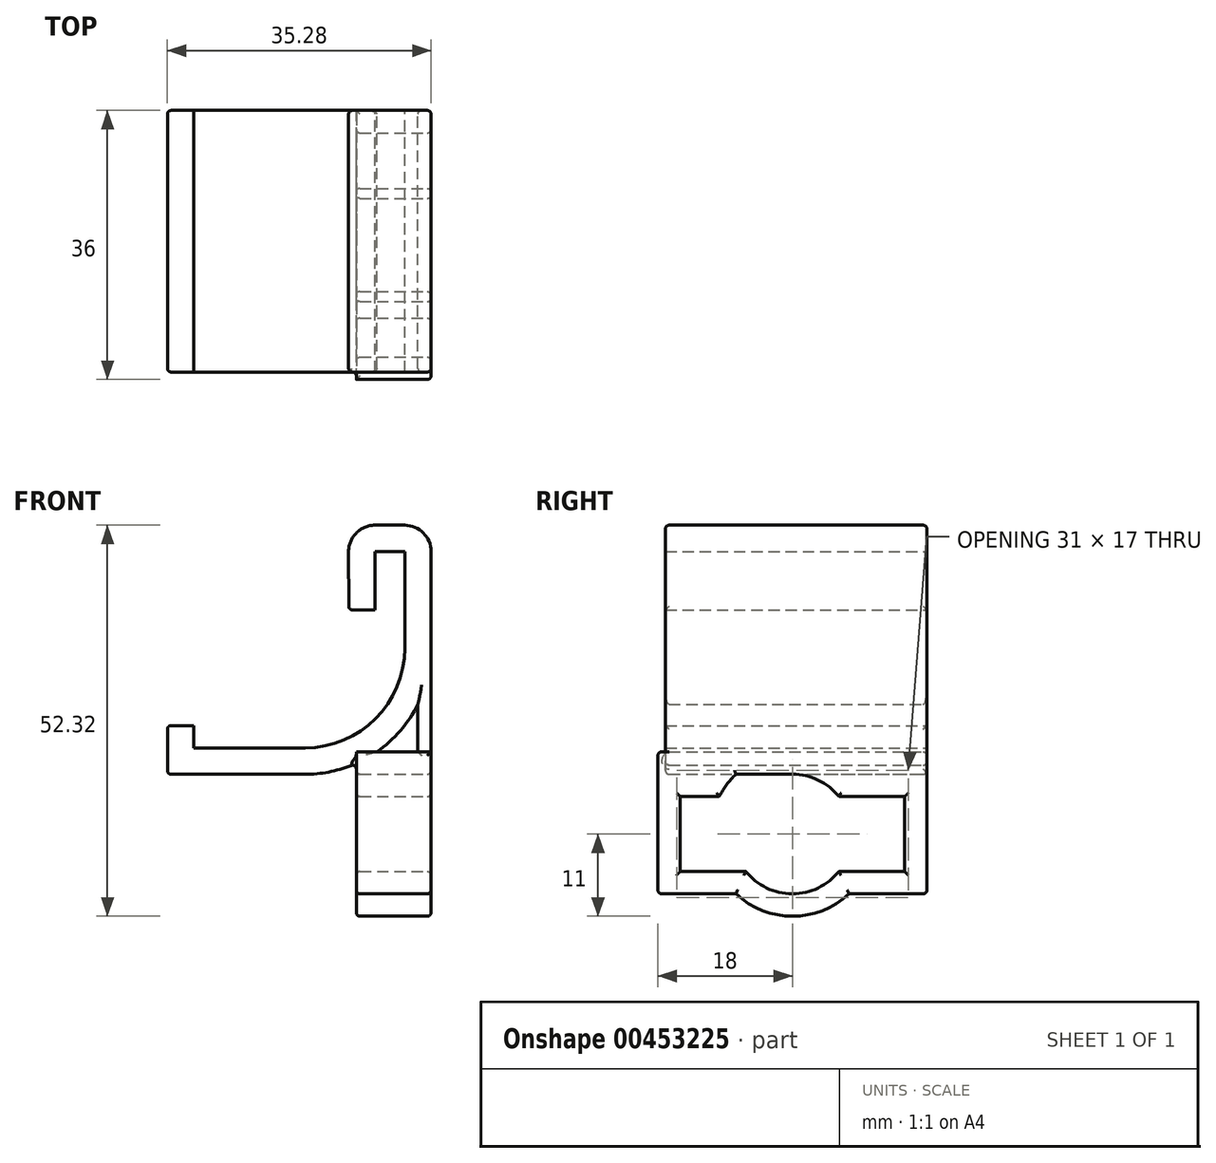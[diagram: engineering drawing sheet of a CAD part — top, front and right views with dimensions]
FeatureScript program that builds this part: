
annotation { "Feature Type Name" : "Feature", "Feature Type Description" : "" }
export const myFeature = defineFeature(function(context is Context, id is Id, definition is map)
    precondition{}
    {
        {
            var Q0;
            Q0=qCreatedBy(makeId("Front.planeOp"),FACE);
            var sketch = newSketch(context, id + "F0", { "sketchPlane" : qUnion([Q0])});
            skLineSegment(sketch, "E0.bottom", {"start": v(-7.52, 22) * mm, "end": v(-11.02, 22) * mm});
            skLineSegment(sketch, "E0.left", {"start": v(-7.52, 22) * mm, "end": v(-7.52, 29.8) * mm});
            skLineSegment(sketch, "E1", {"start": v(-7.52, 29.8) * mm, "end": v(-3.52, 29.8) * mm});
            skLineSegment(sketch, "E2", {"start": v(-3.52, 29.8) * mm, "end": v(-3.52, 16.85) * mm});
            skLineSegment(sketch, "E3", {"start": v(-16.85, 3.52) * mm, "end": v(-31.78, 3.52) * mm});
            skLineSegment(sketch, "E4", {"start": v(-31.78, 3.52) * mm, "end": v(-31.78, 6.52) * mm});
            skLineSegment(sketch, "E5", {"start": v(-31.78, 6.52) * mm, "end": v(-35.28, 6.52) * mm});
            skLineSegment(sketch, "E6", {"start": v(-35.28, 6.52) * mm, "end": v(-35.28, 0) * mm});
            skLineSegment(sketch, "E7", {"start": v(-35.28, 0) * mm, "end": v(-16.85, 0) * mm});
            skLineSegment(sketch, "E8", {"start": v(0, 16.85) * mm, "end": v(0, 29.8) * mm});
            skLineSegment(sketch, "E9", {"start": v(-3.52, 33.32) * mm, "end": v(-7.52, 33.32) * mm});
            skLineSegment(sketch, "E10", {"start": v(-11.02, 22) * mm, "end": v(-11.03, 29.8) * mm});
            skArc(sketch, "E11", {"start": v(-7.52, 33.32) * mm, "mid": v(-10, 32.3) * mm, "end": v(-11.03, 29.8) * mm});
            skArc(sketch, "E12", {"start": v(0, 29.8) * mm, "mid": v(-1.03, 32.3) * mm, "end": v(-3.52, 33.32) * mm});
            skArc(sketch, "E13", {"start": v(0, 16.85) * mm, "mid": v(-4.94, 4.94) * mm, "end": v(-16.85, 0) * mm});
            skArc(sketch, "E14", {"start": v(-3.52, 16.85) * mm, "mid": v(-7.42, 7.42) * mm, "end": v(-16.85, 3.52) * mm});
            skLineSegment(sketch, "E15", {"start": v(0, 16.85) * mm, "end": v(0, 0) * mm});
            skLineSegment(sketch, "E16", {"start": v(0, 0) * mm, "end": v(-1.75, 0) * mm});
            skLineSegment(sketch, "E17", {"start": v(-1.75, 0) * mm, "end": v(-1.75, 9.37) * mm});
            skSolve(sketch);
        }
        {
            var Q0;
            Q0=makeQuery(id+"F0.imprint","IMPRINT",FACE,{"disambiguationData":[TD([[makeQuery(id+"F0.imprint","IMPRINT",EDGE,{"derivedFrom":sQuery(id+"F0.wireOp",EDGE,"E0.bottom")}),-1.0]])]});
            var Q1;
            {var subQ0=sQuery(id+"F0.wireOp",EDGE,"E15");Q1=makeQuery(id+"F0.imprint","IMPRINT",FACE,{"disambiguationData":[TD([[makeQuery(id+"F0.imprint","IMPRINT",EDGE,{"derivedFrom":subQ0}),-1.0]])]});}
            extrude(context, id + "F1", {"entities" : qUnion([Q0, Q1]), "offsetDistance" : 25 * mm, "depth" : 35 * mm});
        }
        {
            var Q0;
            Q0=qCreatedBy(makeId("Right.planeOp"),FACE);
            var sketch = newSketch(context, id + "F2", { "sketchPlane" : qUnion([Q0])});
            skLineSegment(sketch, "E18.bottom", {"start": v(-33, -3) * mm, "end": v(-3, -3) * mm});
            skLineSegment(sketch, "E18.top", {"start": v(-33, -13) * mm, "end": v(-3, -13) * mm});
            skLineSegment(sketch, "E18.left", {"start": v(-33, -3) * mm, "end": v(-33, -13) * mm});
            skLineSegment(sketch, "E18.right", {"start": v(-3, -3) * mm, "end": v(-3, -13) * mm});
            skCircle(sketch, "E19", {"center": v(-18, -8) * mm, "radius": 8 * mm});
            skCircle(sketch, "E20.0", {"center": v(-18, -8) * mm, "radius": 11 * mm});
            skLineSegment(sketch, "E21.0", {"start": v(-36, 0) * mm, "end": v(-36, -16) * mm});
            skLineSegment(sketch, "E21.1", {"start": v(-36, 0) * mm, "end": v(0, 0) * mm});
            skLineSegment(sketch, "E21.2", {"start": v(0, 0) * mm, "end": v(0, -16) * mm});
            skLineSegment(sketch, "E21.3", {"start": v(-36, -16) * mm, "end": v(0, -16) * mm});
            skLineSegment(sketch, "E22", {"start": v(0, 0) * mm, "end": v(0, 3) * mm});
            skLineSegment(sketch, "E23", {"start": v(0, 3) * mm, "end": v(-36, 3) * mm});
            skLineSegment(sketch, "E24", {"start": v(-36, 3) * mm, "end": v(-36, 0) * mm});
            skLineSegment(sketch, "E25", {"start": v(-18, 3) * mm, "end": v(-18, -16) * mm});
            skSolve(sketch);
        }
        {
            var Q0;
            Q0 = qSketchRegion(id + "F2", true);
            var Q1;
            {var subQ0=sQuery(id+"F2.wireOp",EDGE,"E20.0");var subQ1=sQuery(id+"F2.wireOp",EDGE,"E18.bottom");var subQ2=makeQuery(id+"F2.imprint","INTERSECT",VERTEX,{"disambiguationData":[OD(0.0)],"derivedFrom":[subQ1,subQ0]});Q1=makeQuery(id+"F2.imprint","IMPRINT",FACE,{"disambiguationData":[TD([[makeQuery(id+"F2.imprint","IMPRINT",EDGE,{"disambiguationData":[TD([[subQ2,-1.0]])],"derivedFrom":subQ1}),1.0]])]});}
            var Q2;
            {var subQ0=sQuery(id+"F2.wireOp",EDGE,"E19");var subQ1=sQuery(id+"F2.wireOp",EDGE,"E18.bottom");var subQ2=makeQuery(id+"F2.imprint","INTERSECT",VERTEX,{"disambiguationData":[OD(1.0)],"derivedFrom":[subQ1,subQ0]});Q2=makeQuery(id+"F2.imprint","IMPRINT",FACE,{"disambiguationData":[TD([[makeQuery(id+"F2.imprint","IMPRINT",EDGE,{"disambiguationData":[TD([[subQ2,-1.0]])],"derivedFrom":subQ1}),1.0]])]});}
            extrude(context, id + "F3", {"entities" : qUnion([Q0, Q1, Q2]), "depth" : -10 * mm});
        }
        {
            var Q0;
            Q0=makeQuery(id+"F1.opExtrude","SWEPT_BODY",BODY,{"disambiguationData":[OSD([sQuery(id+"F0.wireOp",EDGE,"E0.bottom"),sQuery(id+"F0.wireOp",EDGE,"E0.left"),sQuery(id+"F0.wireOp",EDGE,"E1"),sQuery(id+"F0.wireOp",EDGE,"E2"),sQuery(id+"F0.wireOp",EDGE,"E3"),sQuery(id+"F0.wireOp",EDGE,"E4"),sQuery(id+"F0.wireOp",EDGE,"E5"),sQuery(id+"F0.wireOp",EDGE,"E6"),sQuery(id+"F0.wireOp",EDGE,"E7"),sQuery(id+"F0.wireOp",EDGE,"E8"),sQuery(id+"F0.wireOp",EDGE,"E9"),sQuery(id+"F0.wireOp",EDGE,"E10"),sQuery(id+"F0.wireOp",EDGE,"E11"),sQuery(id+"F0.wireOp",EDGE,"E12"),sQuery(id+"F0.wireOp",EDGE,"E13"),sQuery(id+"F0.wireOp",EDGE,"E14"),sQuery(id+"F0.wireOp",EDGE,"E15"),sQuery(id+"F0.wireOp",EDGE,"E16"),sQuery(id+"F0.wireOp",EDGE,"E17")])]});
            var Q1;
            Q1=makeQuery(id+"F3.opExtrude","SWEPT_BODY",BODY,{"disambiguationData":[OSD([sQuery(id+"F2.wireOp",EDGE,"E18.bottom"),sQuery(id+"F2.wireOp",EDGE,"E18.top"),sQuery(id+"F2.wireOp",EDGE,"E18.left"),sQuery(id+"F2.wireOp",EDGE,"E18.right"),sQuery(id+"F2.wireOp",EDGE,"E19"),sQuery(id+"F2.wireOp",EDGE,"E20.0"),sQuery(id+"F2.wireOp",EDGE,"E21.0"),sQuery(id+"F2.wireOp",EDGE,"E21.2"),sQuery(id+"F2.wireOp",EDGE,"E21.3"),sQuery(id+"F2.wireOp",EDGE,"E22"),sQuery(id+"F2.wireOp",EDGE,"E23"),sQuery(id+"F2.wireOp",EDGE,"E24")])]});
            booleanBodies(context, id + "F4", {"operationType" : BooleanOperationType.UNION, "tools" : qUnion([Q0, Q1])});
        }
        {
            var Q0;
            Q0=makeQuery(id+"F1.opExtrude","CAP_EDGE",EDGE,{"disambiguationData":[OSD([sQuery(id+"F0.wireOp",EDGE,"E12")])],"isStart":false});
            var Q1;
            Q1=makeQuery(id+"F3.opExtrude","SWEPT_EDGE",EDGE,{"disambiguationData":[OSD([sQuery(id+"F2.wireOp",EDGE,"E21.0"),sQuery(id+"F2.wireOp",EDGE,"E21.3")])]});
            var Q2;
            {var subQ0=sQuery(id+"F2.wireOp",EDGE,"E21.3");Q2=makeQuery(id+"F3.opExtrude","CAP_EDGE",EDGE,{"disambiguationData":[OSD([subQ0]),TDD([makeQuery(id+"F2.imprint","IMPRINT",EDGE,{"disambiguationData":[TD([[makeQuery(id+"F2.imprint","INTERSECT",VERTEX,{"derivedFrom":[sQuery(id+"F2.wireOp",EDGE,"E21.0"),subQ0]}),-1.0]])],"derivedFrom":subQ0})])],"isStart":false});}
            var Q3;
            Q3=makeQuery(id+"F3.opExtrude","CAP_EDGE",EDGE,{"disambiguationData":[OSD([sQuery(id+"F2.wireOp",EDGE,"E20.0")])],"isStart":false});
            var Q4;
            {var subQ0=sQuery(id+"F2.wireOp",EDGE,"E19");var subQ1=sQuery(id+"F2.wireOp",EDGE,"E18.bottom");Q4=makeQuery(id+"F3.opExtrude","CAP_EDGE",EDGE,{"disambiguationData":[OSD([subQ0]),TDD([makeQuery(id+"F2.imprint","IMPRINT",EDGE,{"disambiguationData":[TD([[makeQuery(id+"F2.imprint","INTERSECT",VERTEX,{"disambiguationData":[OD(1.0)],"derivedFrom":[subQ1,subQ0]}),-1.0]])],"derivedFrom":subQ0}),makeQuery(id+"F2.imprint","IMPRINT",EDGE,{"disambiguationData":[TD([[makeQuery(id+"F2.imprint","INTERSECT",VERTEX,{"disambiguationData":[OD(0.0)],"derivedFrom":[subQ1,subQ0]}),1.0]])],"derivedFrom":subQ0})])],"isStart":false});}
            var Q5;
            {var subQ0=sQuery(id+"F2.wireOp",EDGE,"E18.bottom");Q5=makeQuery(id+"F3.opExtrude","CAP_EDGE",EDGE,{"disambiguationData":[OSD([subQ0]),TDD([makeQuery(id+"F2.imprint","IMPRINT",EDGE,{"disambiguationData":[TD([[makeQuery(id+"F2.imprint","INTERSECT",VERTEX,{"disambiguationData":[OD(1.0)],"derivedFrom":[subQ0,sQuery(id+"F2.wireOp",EDGE,"E19")]}),-1.0]])],"derivedFrom":subQ0}),makeQuery(id+"F2.imprint","IMPRINT",EDGE,{"disambiguationData":[TD([[makeQuery(id+"F2.imprint","INTERSECT",VERTEX,{"derivedFrom":[subQ0,sQuery(id+"F2.wireOp",EDGE,"E18.right")]}),1.0]])],"derivedFrom":subQ0})])],"isStart":false});}
            var Q6;
            Q6=makeQuery(id+"F3.opExtrude","CAP_EDGE",EDGE,{"disambiguationData":[OSD([sQuery(id+"F2.wireOp",EDGE,"E18.right")])],"isStart":false});
            var Q7;
            {var subQ0=sQuery(id+"F2.wireOp",EDGE,"E18.top");Q7=makeQuery(id+"F3.opExtrude","CAP_EDGE",EDGE,{"disambiguationData":[OSD([subQ0]),TDD([makeQuery(id+"F2.imprint","IMPRINT",EDGE,{"disambiguationData":[TD([[makeQuery(id+"F2.imprint","INTERSECT",VERTEX,{"disambiguationData":[OD(1.0)],"derivedFrom":[subQ0,sQuery(id+"F2.wireOp",EDGE,"E19")]}),-1.0]])],"derivedFrom":subQ0}),makeQuery(id+"F2.imprint","IMPRINT",EDGE,{"disambiguationData":[TD([[makeQuery(id+"F2.imprint","INTERSECT",VERTEX,{"derivedFrom":[subQ0,sQuery(id+"F2.wireOp",EDGE,"E18.right")]}),1.0]])],"derivedFrom":subQ0})])],"isStart":false});}
            var Q8;
            {var subQ0=sQuery(id+"F2.wireOp",EDGE,"E19");var subQ2=sQuery(id+"F2.wireOp",EDGE,"E18.top");Q8=makeQuery(id+"F3.opExtrude","CAP_EDGE",EDGE,{"disambiguationData":[OSD([subQ0]),TDD([makeQuery(id+"F2.imprint","IMPRINT",EDGE,{"disambiguationData":[TD([[makeQuery(id+"F2.imprint","INTERSECT",VERTEX,{"disambiguationData":[OD(0.0)],"derivedFrom":[subQ2,subQ0]}),-1.0]])],"derivedFrom":subQ0}),makeQuery(id+"F2.imprint","IMPRINT",EDGE,{"disambiguationData":[TD([[makeQuery(id+"F2.imprint","INTERSECT",VERTEX,{"disambiguationData":[OD(1.0)],"derivedFrom":[subQ2,subQ0]}),1.0]])],"derivedFrom":subQ0})])],"isStart":false});}
            var Q9;
            {var subQ0=sQuery(id+"F2.wireOp",EDGE,"E18.top");var subQ1=makeQuery(id+"F2.imprint","INTERSECT",VERTEX,{"disambiguationData":[OD(0.0)],"derivedFrom":[subQ0,sQuery(id+"F2.wireOp",EDGE,"E20.0")]});Q9=makeQuery(id+"F3.opExtrude","CAP_EDGE",EDGE,{"disambiguationData":[OSD([subQ0]),TDD([makeQuery(id+"F2.imprint","IMPRINT",EDGE,{"disambiguationData":[TD([[makeQuery(id+"F2.imprint","INTERSECT",VERTEX,{"derivedFrom":[subQ0,sQuery(id+"F2.wireOp",EDGE,"E18.left")]}),-1.0]])],"derivedFrom":subQ0}),makeQuery(id+"F2.imprint","IMPRINT",EDGE,{"disambiguationData":[TD([[subQ1,-1.0]])],"derivedFrom":subQ0})])],"isStart":false});}
            var Q10;
            {var subQ0=sQuery(id+"F2.wireOp",EDGE,"E18.bottom");var subQ1=makeQuery(id+"F2.imprint","INTERSECT",VERTEX,{"disambiguationData":[OD(0.0)],"derivedFrom":[subQ0,sQuery(id+"F2.wireOp",EDGE,"E20.0")]});Q10=makeQuery(id+"F3.opExtrude","CAP_EDGE",EDGE,{"disambiguationData":[OSD([subQ0]),TDD([makeQuery(id+"F2.imprint","IMPRINT",EDGE,{"disambiguationData":[TD([[makeQuery(id+"F2.imprint","INTERSECT",VERTEX,{"derivedFrom":[subQ0,sQuery(id+"F2.wireOp",EDGE,"E18.left")]}),-1.0]])],"derivedFrom":subQ0}),makeQuery(id+"F2.imprint","IMPRINT",EDGE,{"disambiguationData":[TD([[subQ1,-1.0]])],"derivedFrom":subQ0})])],"isStart":false});}
            var Q11;
            Q11=makeQuery(id+"F3.opExtrude","CAP_EDGE",EDGE,{"disambiguationData":[OSD([sQuery(id+"F2.wireOp",EDGE,"E21.0"),sQuery(id+"F2.wireOp",EDGE,"E24")])],"isStart":true});
            var Q12;
            {var subQ0=sQuery(id+"F2.wireOp",EDGE,"E24");var subQ2=sQuery(id+"F0.wireOp",EDGE,"E13");var subQ3=sQuery(id+"F2.wireOp",EDGE,"E23");Q12=makeQuery(id+"F4.opBoolean","SPLIT",EDGE,{"disambiguationData":[TD([makeQuery(id+"F1.opExtrude","SWEPT_FACE",FACE,{"disambiguationData":[OSD([subQ2])]})])],"derivedFrom":makeQuery(id+"F3.opExtrude","SWEPT_EDGE",EDGE,{"disambiguationData":[OSD([subQ3,subQ0])]})});}
            var Q13;
            {var subQ0=sQuery(id+"F0.wireOp",EDGE,"E17");var subQ1=sQuery(id+"F0.wireOp",EDGE,"E13");Q13=makeQuery(id+"F4.opBoolean","SPLIT",EDGE,{"disambiguationData":[TD([makeQuery(id+"F1.opExtrude","SWEPT_FACE",FACE,{"disambiguationData":[OSD([subQ0])]})])],"derivedFrom":makeQuery(id+"F1.opExtrude","CAP_EDGE",EDGE,{"disambiguationData":[OSD([subQ1])],"isStart":false})});}
            var Q14;
            Q14=makeQuery(id+"F1.opExtrude","CAP_EDGE",EDGE,{"disambiguationData":[OSD([sQuery(id+"F0.wireOp",EDGE,"E17")])],"isStart":false});
            var Q15;
            {var subQ2=sQuery(id+"F0.wireOp",EDGE,"E13");var subQ3=sQuery(id+"F0.wireOp",EDGE,"E7");Q15=makeQuery(id+"F4.opBoolean","SPLIT",EDGE,{"disambiguationData":[TD([makeQuery(id+"F1.opExtrude","SWEPT_FACE",FACE,{"disambiguationData":[OSD([subQ3])]})])],"derivedFrom":makeQuery(id+"F1.opExtrude","CAP_EDGE",EDGE,{"disambiguationData":[OSD([subQ2])],"isStart":false})});}
            var Q16;
            {var subQ8=sQuery(id+"F0.wireOp",EDGE,"E13");var subQ14=sQuery(id+"F0.wireOp",EDGE,"E7");Q16=makeQuery(id+"F4.opBoolean","SPLIT",FACE,{"disambiguationData":[TD([makeQuery(id+"F1.opExtrude","SWEPT_FACE",FACE,{"disambiguationData":[OSD([subQ14])]})])],"derivedFrom":makeQuery(id+"F1.opExtrude","SWEPT_FACE",FACE,{"disambiguationData":[OSD([subQ8])]})});}
            var Q17;
            Q17=makeQuery(id+"F1.opExtrude","SWEPT_EDGE",EDGE,{"disambiguationData":[OSD([sQuery(id+"F0.wireOp",EDGE,"E6"),sQuery(id+"F0.wireOp",EDGE,"E7")])]});
            var Q18;
            {var subQ0=sQuery(id+"F0.wireOp",EDGE,"E17");var subQ1=sQuery(id+"F0.wireOp",EDGE,"E13");Q18=makeQuery(id+"F4.opBoolean","SPLIT",EDGE,{"disambiguationData":[TD([makeQuery(id+"F1.opExtrude","SWEPT_FACE",FACE,{"disambiguationData":[OSD([subQ0])]})])],"derivedFrom":makeQuery(id+"F1.opExtrude","CAP_EDGE",EDGE,{"disambiguationData":[OSD([subQ1])],"isStart":true})});}
            var Q19;
            {var subQ0=sQuery(id+"F2.wireOp",EDGE,"E22");var subQ2=sQuery(id+"F0.wireOp",EDGE,"E13");var subQ3=sQuery(id+"F2.wireOp",EDGE,"E23");Q19=makeQuery(id+"F4.opBoolean","SPLIT",EDGE,{"disambiguationData":[TD([makeQuery(id+"F1.opExtrude","SWEPT_FACE",FACE,{"disambiguationData":[OSD([subQ2])]})])],"derivedFrom":makeQuery(id+"F3.opExtrude","SWEPT_EDGE",EDGE,{"disambiguationData":[OSD([subQ0,subQ3])]})});}
            var Q20;
            Q20=makeQuery(id+"F1.opExtrude","CAP_EDGE",EDGE,{"disambiguationData":[OSD([sQuery(id+"F0.wireOp",EDGE,"E17")])],"isStart":true});
            var Q21;
            Q21=makeQuery(id+"F1.opExtrude","CAP_EDGE",EDGE,{"disambiguationData":[OSD([sQuery(id+"F0.wireOp",EDGE,"E12")])],"isStart":true});
            var Q22;
            Q22=makeQuery(id+"F3.opExtrude","SWEPT_EDGE",EDGE,{"disambiguationData":[OSD([sQuery(id+"F2.wireOp",EDGE,"E21.2"),sQuery(id+"F2.wireOp",EDGE,"E21.3")])]});
            var Q23;
            {var subQ0=sQuery(id+"F2.wireOp",EDGE,"E21.3");Q23=makeQuery(id+"F3.opExtrude","CAP_EDGE",EDGE,{"disambiguationData":[OSD([subQ0]),TDD([makeQuery(id+"F2.imprint","IMPRINT",EDGE,{"disambiguationData":[TD([[makeQuery(id+"F2.imprint","INTERSECT",VERTEX,{"derivedFrom":[sQuery(id+"F2.wireOp",EDGE,"E21.2"),subQ0]}),1.0]])],"derivedFrom":subQ0})])],"isStart":true});}
            var Q24;
            Q24=makeQuery(id+"F3.opExtrude","CAP_EDGE",EDGE,{"disambiguationData":[OSD([sQuery(id+"F2.wireOp",EDGE,"E20.0")])],"isStart":true});
            var Q25;
            {var subQ0=sQuery(id+"F2.wireOp",EDGE,"E21.3");Q25=makeQuery(id+"F3.opExtrude","CAP_EDGE",EDGE,{"disambiguationData":[OSD([subQ0]),TDD([makeQuery(id+"F2.imprint","IMPRINT",EDGE,{"disambiguationData":[TD([[makeQuery(id+"F2.imprint","INTERSECT",VERTEX,{"derivedFrom":[sQuery(id+"F2.wireOp",EDGE,"E21.0"),subQ0]}),-1.0]])],"derivedFrom":subQ0})])],"isStart":true});}
            var Q26;
            {var subQ0=sQuery(id+"F2.wireOp",EDGE,"E21.3");Q26=makeQuery(id+"F3.opExtrude","CAP_EDGE",EDGE,{"disambiguationData":[OSD([subQ0]),TDD([makeQuery(id+"F2.imprint","IMPRINT",EDGE,{"disambiguationData":[TD([[makeQuery(id+"F2.imprint","INTERSECT",VERTEX,{"derivedFrom":[sQuery(id+"F2.wireOp",EDGE,"E21.2"),subQ0]}),1.0]])],"derivedFrom":subQ0})])],"isStart":false});}
            var Q27;
            Q27=makeQuery(id+"F1.opExtrude","CAP_EDGE",EDGE,{"disambiguationData":[OSD([sQuery(id+"F0.wireOp",EDGE,"E6")])],"isStart":false});
            var Q28;
            Q28=makeQuery(id+"F1.opExtrude","CAP_EDGE",EDGE,{"disambiguationData":[OSD([sQuery(id+"F0.wireOp",EDGE,"E6")])],"isStart":true});
            var Q29;
            Q29=makeQuery(id+"F3.opExtrude","CAP_EDGE",EDGE,{"disambiguationData":[OSD([sQuery(id+"F2.wireOp",EDGE,"E18.left")])],"isStart":false});
            var Q30;
            Q30=makeQuery(id+"F3.opExtrude","CAP_EDGE",EDGE,{"disambiguationData":[OSD([sQuery(id+"F2.wireOp",EDGE,"E18.left")])],"isStart":true});
            var Q31;
            {var subQ0=sQuery(id+"F2.wireOp",EDGE,"E18.bottom");var subQ1=makeQuery(id+"F2.imprint","INTERSECT",VERTEX,{"disambiguationData":[OD(0.0)],"derivedFrom":[subQ0,sQuery(id+"F2.wireOp",EDGE,"E20.0")]});Q31=makeQuery(id+"F3.opExtrude","CAP_EDGE",EDGE,{"disambiguationData":[OSD([subQ0]),TDD([makeQuery(id+"F2.imprint","IMPRINT",EDGE,{"disambiguationData":[TD([[makeQuery(id+"F2.imprint","INTERSECT",VERTEX,{"derivedFrom":[subQ0,sQuery(id+"F2.wireOp",EDGE,"E18.left")]}),-1.0]])],"derivedFrom":subQ0}),makeQuery(id+"F2.imprint","IMPRINT",EDGE,{"disambiguationData":[TD([[subQ1,-1.0]])],"derivedFrom":subQ0})])],"isStart":true});}
            var Q32;
            {var subQ0=sQuery(id+"F2.wireOp",EDGE,"E19");var subQ1=sQuery(id+"F2.wireOp",EDGE,"E18.bottom");Q32=makeQuery(id+"F3.opExtrude","CAP_EDGE",EDGE,{"disambiguationData":[OSD([subQ0]),TDD([makeQuery(id+"F2.imprint","IMPRINT",EDGE,{"disambiguationData":[TD([[makeQuery(id+"F2.imprint","INTERSECT",VERTEX,{"disambiguationData":[OD(1.0)],"derivedFrom":[subQ1,subQ0]}),-1.0]])],"derivedFrom":subQ0}),makeQuery(id+"F2.imprint","IMPRINT",EDGE,{"disambiguationData":[TD([[makeQuery(id+"F2.imprint","INTERSECT",VERTEX,{"disambiguationData":[OD(0.0)],"derivedFrom":[subQ1,subQ0]}),1.0]])],"derivedFrom":subQ0})])],"isStart":true});}
            var Q33;
            {var subQ0=sQuery(id+"F2.wireOp",EDGE,"E18.bottom");Q33=makeQuery(id+"F3.opExtrude","CAP_EDGE",EDGE,{"disambiguationData":[OSD([subQ0]),TDD([makeQuery(id+"F2.imprint","IMPRINT",EDGE,{"disambiguationData":[TD([[makeQuery(id+"F2.imprint","INTERSECT",VERTEX,{"disambiguationData":[OD(1.0)],"derivedFrom":[subQ0,sQuery(id+"F2.wireOp",EDGE,"E19")]}),-1.0]])],"derivedFrom":subQ0}),makeQuery(id+"F2.imprint","IMPRINT",EDGE,{"disambiguationData":[TD([[makeQuery(id+"F2.imprint","INTERSECT",VERTEX,{"derivedFrom":[subQ0,sQuery(id+"F2.wireOp",EDGE,"E18.right")]}),1.0]])],"derivedFrom":subQ0})])],"isStart":true});}
            var Q34;
            Q34=makeQuery(id+"F3.opExtrude","CAP_EDGE",EDGE,{"disambiguationData":[OSD([sQuery(id+"F2.wireOp",EDGE,"E18.right")])],"isStart":true});
            var Q35;
            {var subQ0=sQuery(id+"F2.wireOp",EDGE,"E18.top");Q35=makeQuery(id+"F3.opExtrude","CAP_EDGE",EDGE,{"disambiguationData":[OSD([subQ0]),TDD([makeQuery(id+"F2.imprint","IMPRINT",EDGE,{"disambiguationData":[TD([[makeQuery(id+"F2.imprint","INTERSECT",VERTEX,{"disambiguationData":[OD(1.0)],"derivedFrom":[subQ0,sQuery(id+"F2.wireOp",EDGE,"E19")]}),-1.0]])],"derivedFrom":subQ0}),makeQuery(id+"F2.imprint","IMPRINT",EDGE,{"disambiguationData":[TD([[makeQuery(id+"F2.imprint","INTERSECT",VERTEX,{"derivedFrom":[subQ0,sQuery(id+"F2.wireOp",EDGE,"E18.right")]}),1.0]])],"derivedFrom":subQ0})])],"isStart":true});}
            var Q36;
            {var subQ0=sQuery(id+"F2.wireOp",EDGE,"E19");var subQ2=sQuery(id+"F2.wireOp",EDGE,"E18.top");Q36=makeQuery(id+"F3.opExtrude","CAP_EDGE",EDGE,{"disambiguationData":[OSD([subQ0]),TDD([makeQuery(id+"F2.imprint","IMPRINT",EDGE,{"disambiguationData":[TD([[makeQuery(id+"F2.imprint","INTERSECT",VERTEX,{"disambiguationData":[OD(0.0)],"derivedFrom":[subQ2,subQ0]}),-1.0]])],"derivedFrom":subQ0}),makeQuery(id+"F2.imprint","IMPRINT",EDGE,{"disambiguationData":[TD([[makeQuery(id+"F2.imprint","INTERSECT",VERTEX,{"disambiguationData":[OD(1.0)],"derivedFrom":[subQ2,subQ0]}),1.0]])],"derivedFrom":subQ0})])],"isStart":true});}
            var Q37;
            {var subQ0=sQuery(id+"F2.wireOp",EDGE,"E18.top");var subQ1=makeQuery(id+"F2.imprint","INTERSECT",VERTEX,{"disambiguationData":[OD(0.0)],"derivedFrom":[subQ0,sQuery(id+"F2.wireOp",EDGE,"E20.0")]});Q37=makeQuery(id+"F3.opExtrude","CAP_EDGE",EDGE,{"disambiguationData":[OSD([subQ0]),TDD([makeQuery(id+"F2.imprint","IMPRINT",EDGE,{"disambiguationData":[TD([[makeQuery(id+"F2.imprint","INTERSECT",VERTEX,{"derivedFrom":[subQ0,sQuery(id+"F2.wireOp",EDGE,"E18.left")]}),-1.0]])],"derivedFrom":subQ0}),makeQuery(id+"F2.imprint","IMPRINT",EDGE,{"disambiguationData":[TD([[subQ1,-1.0]])],"derivedFrom":subQ0})])],"isStart":true});}
            var Q38;
            Q38=makeQuery(id+"F1.opExtrude","SWEPT_EDGE",EDGE,{"disambiguationData":[OSD([sQuery(id+"F0.wireOp",EDGE,"E5"),sQuery(id+"F0.wireOp",EDGE,"E6")])]});
            var Q39;
            Q39=makeQuery(id+"F1.opExtrude","SWEPT_EDGE",EDGE,{"disambiguationData":[OSD([sQuery(id+"F0.wireOp",EDGE,"E0.bottom"),sQuery(id+"F0.wireOp",EDGE,"E10")])]});
            fillet(context, id + "F5", {"entities" : qUnion([Q0, Q1, Q2, Q3, Q4, Q5, Q6, Q7, Q8, Q9, Q10, Q11, Q12, Q13, Q14, Q15, Q16, Q17, Q18, Q19, Q20, Q21, Q22, Q23, Q24, Q25, Q26, Q27, Q28, Q29, Q30, Q31, Q32, Q33, Q34, Q35, Q36, Q37, Q38, Q39]), "radius" : 0.5 * mm, "tangentPropagation" : true, "allowEdgeOverflow" : false});
        }
    });
